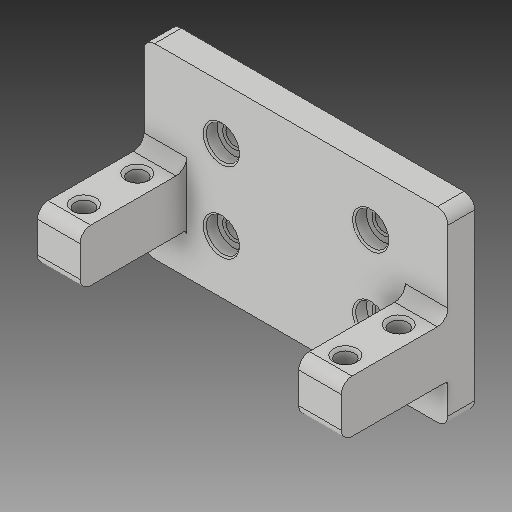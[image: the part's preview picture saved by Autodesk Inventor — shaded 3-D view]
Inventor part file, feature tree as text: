
AUTODESK INVENTOR PART (.ipt)
format: ipt  version: 2019 (Build 230136000, 136)  size: 274,944 bytes
history: native  units: mm
features: extrude x4, fillet x4, sketch x4, chamfer x2, thicken_offset x2
ambient origin geometry x8: Origin, YZ Plane, XZ Plane, XY Plane, X Axis, Y Axis, Z Axis, Center Point
bodies: Solid1 (feature_tree)
feature tree (16):
  extrude  "Extrusion1"  Depth=15.0mm
  extrude  "Extrusion2"  Depth=35.0mm
  extrude  "Extrusion4"  Depth=5.0mm
  fillet  "Fillet2"  Radius=3.5mm
  fillet  "Fillet3"  Radius=3.5mm
  fillet  "Fillet4"  Radius=5.0mm
  chamfer  "Chamfer1"  Distance=20.5mm
  chamfer  "Chamfer2"  Distance=7.0mm
  extrude  "Extrusion5"  Depth=9.8mm
  fillet  "Fillet5"  Radius=20.0mm
  thicken_offset  "Thicken1"
  thicken_offset  "Thicken2"
  sketch  "Sketch1"  dims[d0=28.0mm d1=15.0mm]
  sketch  "Sketch2"  dims[d2=55.0mm d3=35.0mm]
  sketch  "Sketch4"  dims[d4=3.5mm d5=3.5mm d6=3.5mm d7=3.5mm d8=5.0mm d9=0.0mm]
  sketch  "Sketch5"  dims[d10=10.0mm d11=20.5mm d12=7.0mm d13=9.8mm d14=20.0mm d15=0.0mm d26=24.5mm d27=10.25mm d28=3.4mm d29=10.0mm d30=90.0deg d31=3.4mm d32=10.0mm d33=0.0mm d34=2.0mm d35=0.5mm d36=2.0mm d37=0.5mm d38=2.0mm d39=45.0deg d40=0.5mm d41=2.0mm d42=45.0deg d46=6.2mm d47=6.2mm d48=6.2mm d49=6.2mm d50=2.3mm d51=0.0mm d52=0.3mm d53=1.0mm d54=1.0mm d55=1.0mm d56=1.0mm]
